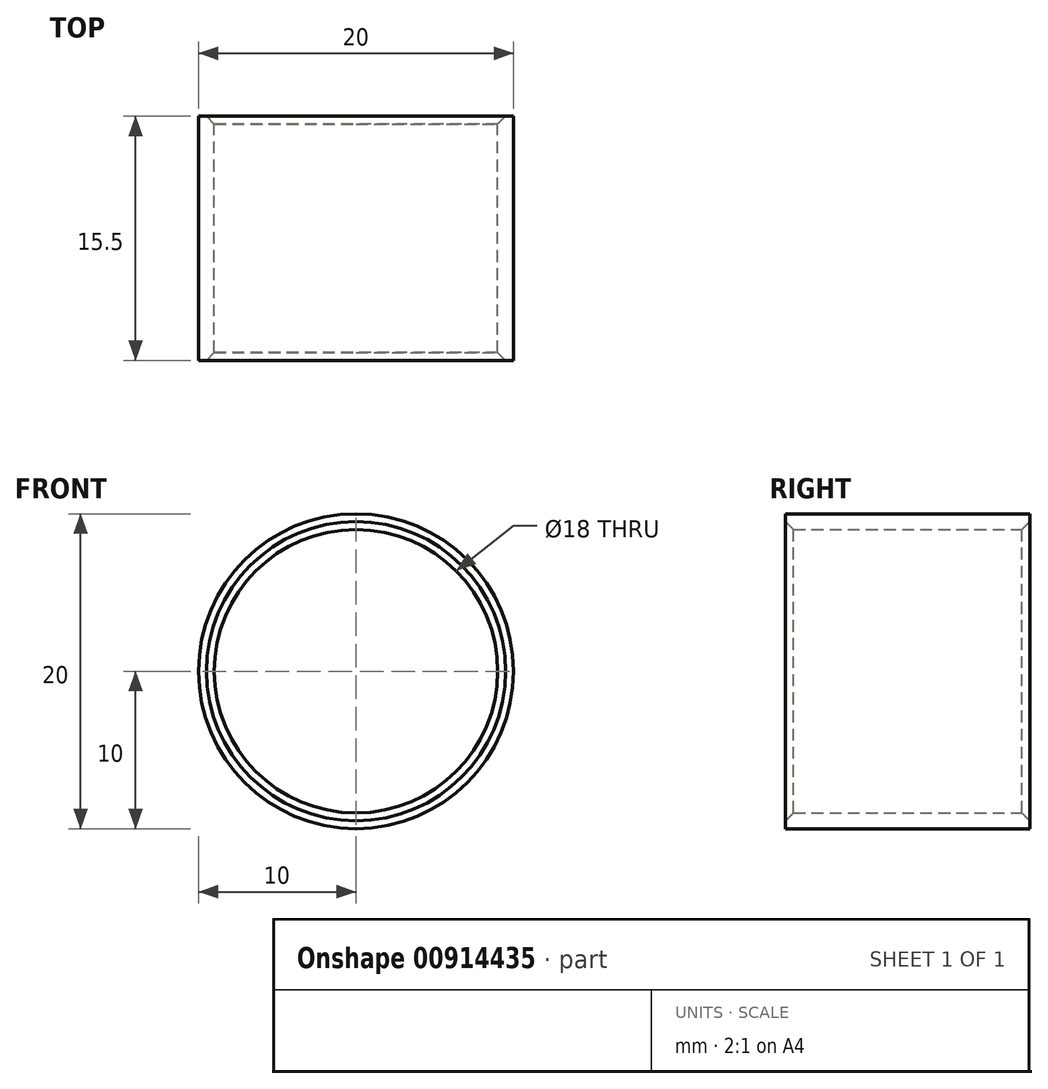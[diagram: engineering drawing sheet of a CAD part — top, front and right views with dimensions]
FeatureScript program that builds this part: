
annotation { "Feature Type Name" : "Feature", "Feature Type Description" : "" }
export const myFeature = defineFeature(function(context is Context, id is Id, definition is map)
    precondition{}
    {
        {
            var Q0;
            Q0=qCreatedBy(makeId("Front.planeOp"),FACE);
            var sketch = newSketch(context, id + "F0", { "sketchPlane" : qUnion([Q0])});
            skCircle(sketch, "E0", {"center": v(0, 0) * mm, "radius": 9 * mm});
            skCircle(sketch, "E1.0", {"center": v(0, 0) * mm, "radius": 10 * mm});
            skSolve(sketch);
        }
        {
            var Q0;
            Q0 = qSketchRegion(id + "F0", true);
            extrude(context, id + "F1", {"entities" : qUnion([Q0]), "depth" : 15.5 * mm, "offsetDistance" : 25 * mm});
        }
        {
            var Q0;
            Q0=makeQuery(id+"F1.opExtrude","SWEPT_FACE",FACE,{"disambiguationData":[OSD([sQuery(id+"F0.wireOp",EDGE,"E0")])]});
            chamfer(context, id + "F2", {"entities" : qUnion([Q0]), "width" : .5 * mm, "tangentPropagation" : true});
        }
    });
